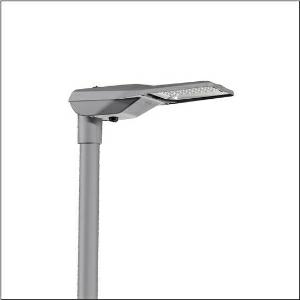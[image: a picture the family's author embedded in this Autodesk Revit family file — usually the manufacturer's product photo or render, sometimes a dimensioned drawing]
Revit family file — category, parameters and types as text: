
# Revit family: streetlight_sl_21_mini___st1_0ab_5xe2m33t08jb_4ee1
name_source: partatom
category: Lighting Fixtures
units: mm (PartAtom-declared; Revit-internal decimal feet)

## family parameters
Cut with Voids When Loaded = No
Host = Face
Light Source = No
Part Type = Normal
Room Calculation Point = No
Round Connector Dimension = Use Diameter
Shared = No

## types (1)
- --- (1 x LED, 11390 lm, 88.6 W, 3000K)
    Apparent Load = 89 VA
    CIE Flux Codes = 40 74 97 100 100
    Color Rendering = 70
    Color Temperature = 3000K
    Default Elevation = 1800 mm
    Description = Streetlight SL 21 mini, mast luminaire, primary light control with lens, of PMMA, primary optical cover: cover, of toughened safety glass, transparent, light distribution: ST1.0aB, light emission: direct distribution, primary light characteristic: asymmetric, installation type: side-entry, post-top, LED, High Power LED, rated luminous flux: 11.390lm, luminous efficacy: 129lm/W, light colour: 730, colour temperature: 3000K, control gear: D4i, control: flexible luminous flux parameterisation, time-dependent luminous flux control, constant luminous flux control, overheat protection, pre-setting: logarithmic dimming characteristic, mains connection: 220..240V, AC, 50/60Hz, start of lifetime: 89W, end of service life: 92W, reduction: 41W, luminaire housing, of diecast aluminium, powder-coated, Siteco® metallic grey (DB 702S), corrosivity category C5 mid according to DIN EN ISO 12944, please order mast flange separately, inclination adjustable: 0°, 5°, 10°, 15°, sealing non-destructively replaceable, multi-level sealing system, length: 628mm, width: 235mm, height: 110mm, mast flange for spigot size: 42mm (side-entry): 5XC10008XM4, 60/48mm (side-entry/post-top): 5XC10108XM2, 76/60mm (side-entry/post-top): 5XC10108XM1, mounting height: 4..8m, Smart Interface below and above, protection rating (complete): IP66, insulation class (complete): insulation class II (safety insulation), certification: CE, ENEC, ENEC+, VDE, impact resistance: IK10, permissible operating ambient temperature for outdoor applications: -40..+50°C, standard-compliant lighting for roads and squares, packaging unit: 1 piece

Light Distribution: ST1.0aB
    Height = 110 mm
    Lamp = 1 x LED
    Lamp Light Flux = 11390 lm
    Lamp Power = 88.6 W
    Lamp count = 1
    Length = 625 mm
    Luminous efficacy = 129 lm/W
    Manufacturer = Siteco
    ModVariant = No
    Model = 5XE2M33T08JB
    Number of Poles = 1
    OnlyDefault = Yes
    Power Factor = 1
    Product Name = Streetlight SL 21 mini | ST1.0aB
    Product group = mast luminaire | pylon top
    ProductGroupID = 6100
    Protection Class = Protection class II
    Protection Degree = IP 66
    RLX_Detail_Level = 1
    RLX_Emergency_Light_Flux = 0 lm
    RLX_Emergency_Type = 0
    RLX_Emergency_Type_DB = No
    RlxData = <blob elided: 26361 chars, md5=e1829e16>
    Socket = socket
    Standby Power = 0 W
    System Light Flux = 11390 lm
    System Power = 89 W
    Type Comments = factory setting: luminous flux: 100 % | dim-lin: 254 | 915 mA
    Type Image = l_1003514.jpg
    URL = http://relux.com
    VarID = @adj_030717
    Voltage = 0 V
    Weight = 0.00 kg
    Width = 234 mm

## geometry (parser evidence)
native form markers: Blend x4, Sweep x9
no freeform markers — native parametric forms only
